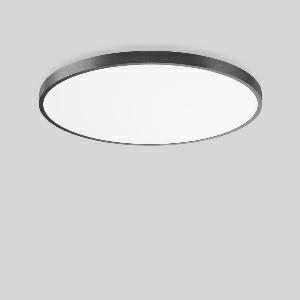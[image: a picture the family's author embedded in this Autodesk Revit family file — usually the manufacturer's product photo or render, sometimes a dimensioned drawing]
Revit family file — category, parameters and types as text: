
# Revit family: triona_round_a_312391_0031_730_7176
name_source: partatom
category: Lighting Fixtures
units: mm (PartAtom-declared; Revit-internal decimal feet)

## family parameters
Cut with Voids When Loaded = No
Host = Face
Light Source = No
Part Type = Normal
Room Calculation Point = No
Round Connector Dimension = Use Diameter
Shared = No

## types (1)
- TRIONA round A (1 x LED Modul 830, 11200 lm, 3000)
    Apparent Load = 106 VA
    CIE Flux Codes = 49 80 96 100 100
    Color Rendering = 80
    Color Temperature = 3000
    Default Elevation = 1800 mm
    Description = Series: TRIONA round
Decorative round LED surface-mounted luminaire. Flat, seamless frame: aluminium extrusion profile, powder coated. Cover made of sheet steel, powder-coated. Light emission through a diffuser: plastic, opal. Lightguide and diffuser made of non-yellowing plastic (PMMA). Lateral light emission (RZB SIDELITE technology) for above-average homogeneous light distribution. Suitable for Ceiling mounting, Wall (surface). Tool-free mounting via bayonet connection. Electronic ballast included. Very easy installation thanks to Plug+Play connection. With Casambi smart+free Bluetooth control for wireless network and operation using Android / iOS devices, free app available for download. 
Colour: anthracite metallic (DB703)
Diameter: 1009 mm
Height: 88 mm
Lamp: LED
Socket: without socket
Colour temperature: 3000K
Colour rendering index (CRI): 80
System power: 106 W
Rated luminous flux: 11200 lm
Luminous efficiency: 106 lm/W
Control gear: Dimmable Bluetooth converter
Protection class: I
Type of protection: IP 20
    Height = 88 mm
    Lamp = 1 x LED Modul 830
    Lamp Light Flux = 11200 lm
    Lamp count = 1
    Length = 1009 mm
    Lifetime = 50000 h
    Luminous efficacy = 106 lm/W
    Manufacturer = RZB
    ModVariant = No
    Model = 312391.0031.730
    Mounting Place = Ceiling
    Mounting Type = Surface mounted
    Number of Poles = 1
    OnlyDefault = Yes
    Power Factor = 1
    Product Name = TRIONA round A
    Product group = Surface mounted modular luminaires
    ProductGroupID = 306
    Protection Class = Protection class I
    Protection Degree = IP 20
    RLX_Detail_Level = 1
    RLX_Emergency_Light_Flux = 0 lm
    RLX_Emergency_Type = 0
    RLX_Emergency_Type_DB = No
    RlxData = <blob elided: 40425 chars, md5=50e592a8>
    Socket = socket
    Standby Power = 0 W
    System Light Flux = 11200 lm
    System Power = 106 W
    Type Comments = Product without accessories
    Type Image = 312392.0031.jpg
    URL = http://relux.com
    VarID = ---
    Voltage = 230 V
    Voltage Range = 220-240 V
    Weight = 0.00 kg
    Width = 0 mm  [stored 0 ft]

note: [stored X ft] marks values corroborated as IEEE doubles in the binary element streams (Revit-internal decimal feet)

## geometry (parser evidence)
native form markers: Blend x4, Sweep x11
no freeform markers — native parametric forms only
